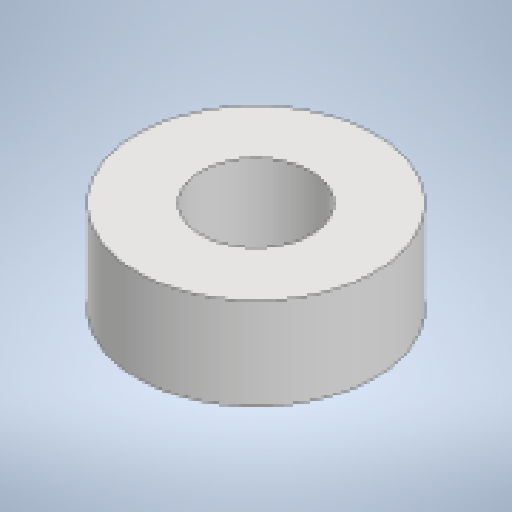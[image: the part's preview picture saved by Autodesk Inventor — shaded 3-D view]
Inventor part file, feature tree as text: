
AUTODESK INVENTOR PART (.ipt)
format: ipt  version: 2023 (Build 270158000, 158)  size: 129,536 bytes
history: native  units: in
note: dims shown in document units (in); Inventor stores cm internally (conversion verified against a paired STEP export)
features: extrude x1, sketch x1
ambient origin geometry x8: Origin, YZ Plane, XZ Plane, XY Plane, X Axis, Y Axis, Z Axis, Center Point
bodies: Solid1 (feature_tree)
feature tree (2):
  extrude  "Extrusion1"  Depth=0.1969in
  sketch  "Sketch1"  dims[d0=0.5118in d1=0.2362in d2=0.1969in d3=0.0in]
